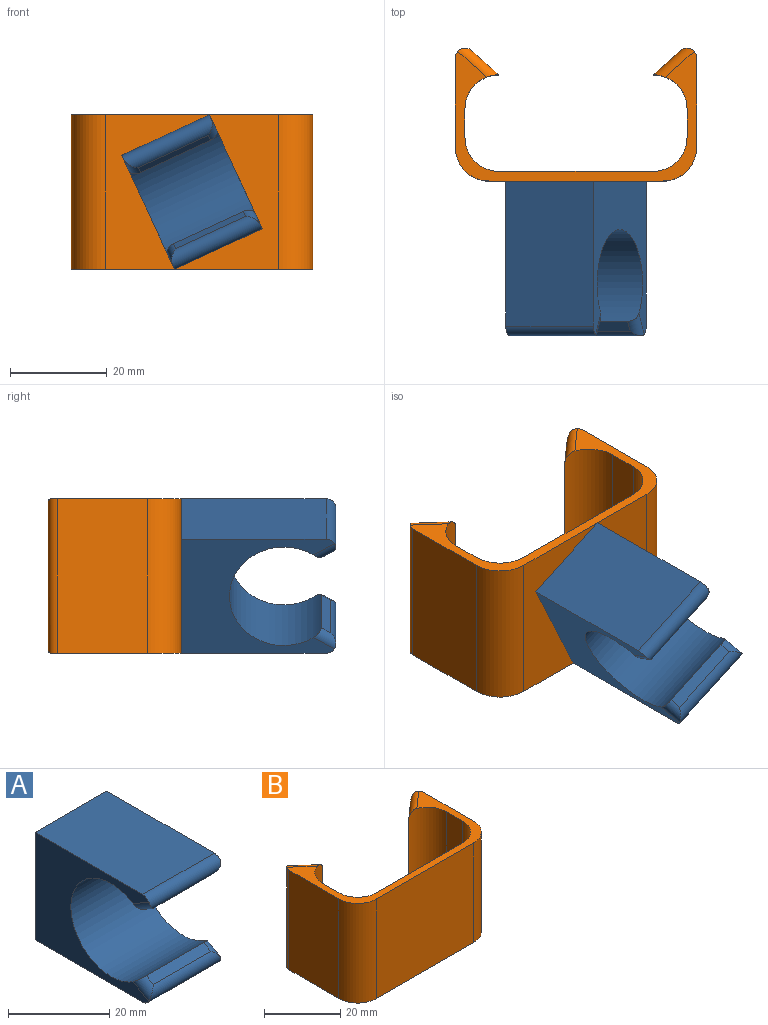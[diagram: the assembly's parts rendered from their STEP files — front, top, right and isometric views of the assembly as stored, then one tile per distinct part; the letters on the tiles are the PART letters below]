
ASSEMBLY  parts=2 mates=1
PART A: 14 faces, bbox 20x32.8x26 mm
  f0: plane 26x20mm, normal (0,1,0), area 520mm2, adj f1,f5,f6,f7
  f1: plane 30.04x20mm, normal (0,0,1), area 600.7mm2, adj f0,f6,f7,f10
  f2: plane 16x2mm, normal (0,-0.5,-0.87), area 36.9mm2, adj f3,f8,f9,f10
  f3: cylinder r=11.25mm len=22.5mm, axis (-1,0,0), area 1047.5mm2, adj f2,f4,f6,f7,f8,f9,f11,f12
  f4: plane 16x2mm, normal (0,-0.5,0.87), area 36.9mm2, adj f3,f11,f12,f13
  f5: plane 30.04x20mm, normal (0,0,-1), area 600.7mm2, adj f0,f6,f7,f13
  f6: plane 31.77x26mm, normal (1,0,0), area 401.2mm2, adj f0,f1,f3,f5,f8,f10,f11,f13
  f7: plane 31.77x26mm, normal (-1,0,0), area 401.2mm2, adj f0,f1,f3,f5,f9,f10,f12,f13
  f8: cylinder r=2mm len=5.42mm, axis (0,-0.87,0.5), area 12mm2, adj f2,f3,f6,f10
  f9: cylinder r=2mm len=5.42mm, axis (0,0.87,-0.5), area 12mm2, adj f2,f3,f7,f10
  f10: cylinder r=2mm len=20mm, axis (1,0,0), area 100.2mm2, adj f1,f2,f6,f7,f8,f9
  f11: cylinder r=2mm len=5.42mm, axis (0,0.87,0.5), area 12mm2, adj f3,f4,f6,f13
  f12: cylinder r=2mm len=5.42mm, axis (0,-0.87,-0.5), area 12mm2, adj f3,f4,f7,f13
  f13: cylinder r=2mm len=20mm, axis (1,0,0), area 100.2mm2, adj f4,f5,f6,f7,f11,f12
PART B: 22 faces, bbox 50x28.4x32 mm
  f0: cylinder r=7mm len=32mm, axis (0,0,1), area 351.9mm2, adj f1,f13,f14,f15
  f1: plane 32x6mm, normal (1,0,0), area 192mm2, adj f0,f2,f14,f15
  f2: cylinder r=7mm len=32mm, axis (0,0,1), area 349.5mm2, adj f1,f3,f14,f15,f16,f17
  f3: plane 28x5.67mm, normal (0.66,0.75,0), area 212.5mm2, adj f2,f16,f17,f18
  f4: plane 32x18.55mm, normal (-1,0,0), area 593.5mm2, adj f5,f14,f15,f18
  f5: cylinder r=7mm len=32mm, axis (0,0,1), area 351.9mm2, adj f4,f6,f14,f15
  f6: plane 36x32mm, normal (0,-1,0), area 1152mm2, adj f5,f7,f14,f15
  f7: cylinder r=7mm len=32mm, axis (0,0,1), area 351.9mm2, adj f6,f8,f14,f15
  f8: plane 32x18.55mm, normal (1,0,0), area 593.5mm2, adj f7,f14,f15,f21
  f9: plane 28x5.67mm, normal (-0.66,0.75,0), area 212.5mm2, adj f10,f19,f20,f21
  f10: cylinder r=7mm len=32mm, axis (0,0,1), area 349.5mm2, adj f9,f11,f14,f15,f19,f20
  f11: plane 32x6mm, normal (-1,0,0), area 192mm2, adj f10,f12,f14,f15
  f12: cylinder r=7mm len=32mm, axis (0,0,1), area 351.9mm2, adj f11,f13,f14,f15
  f13: plane 32x32mm, normal (0,1,0), area 1024mm2, adj f0,f12,f14,f15
  f14: plane 50x26.88mm, normal (0,0,-1), area 231.3mm2, adj f0,f1,f2,f4,f5,f6,f7,f8
  f15: plane 50x26.88mm, normal (0,0,1), area 231.3mm2, adj f0,f1,f2,f4,f5,f6,f7,f8
  f16: cylinder r=2mm len=8.5mm, axis (0.75,-0.66,0), area 25.8mm2, adj f2,f3,f14,f18
  f17: cylinder r=2mm len=8.5mm, axis (-0.75,0.66,0), area 25.8mm2, adj f2,f3,f15,f18
  f18: cylinder r=2mm len=32mm, axis (0,0,-1), area 142.5mm2, adj f3,f4,f14,f15,f16,f17
  f19: cylinder r=2mm len=8.5mm, axis (0.75,0.66,0), area 25.8mm2, adj f9,f10,f14,f21
  f20: cylinder r=2mm len=8.5mm, axis (-0.75,-0.66,0), area 25.8mm2, adj f9,f10,f15,f21
  f21: cylinder r=2mm len=32mm, axis (0,0,1), area 142.5mm2, adj f8,f9,f14,f15,f19,f20
PLACE A rot(axis=(0,-1,0),24.8deg) t=(0.09,-2.08,0.08)mm
PLACE B t=(0.09,-2.08,0.08)mm
MATE fastened A.f0 <-> B.f6  axis (0,1,0) through (0.09,-2.08,0.08)mm
